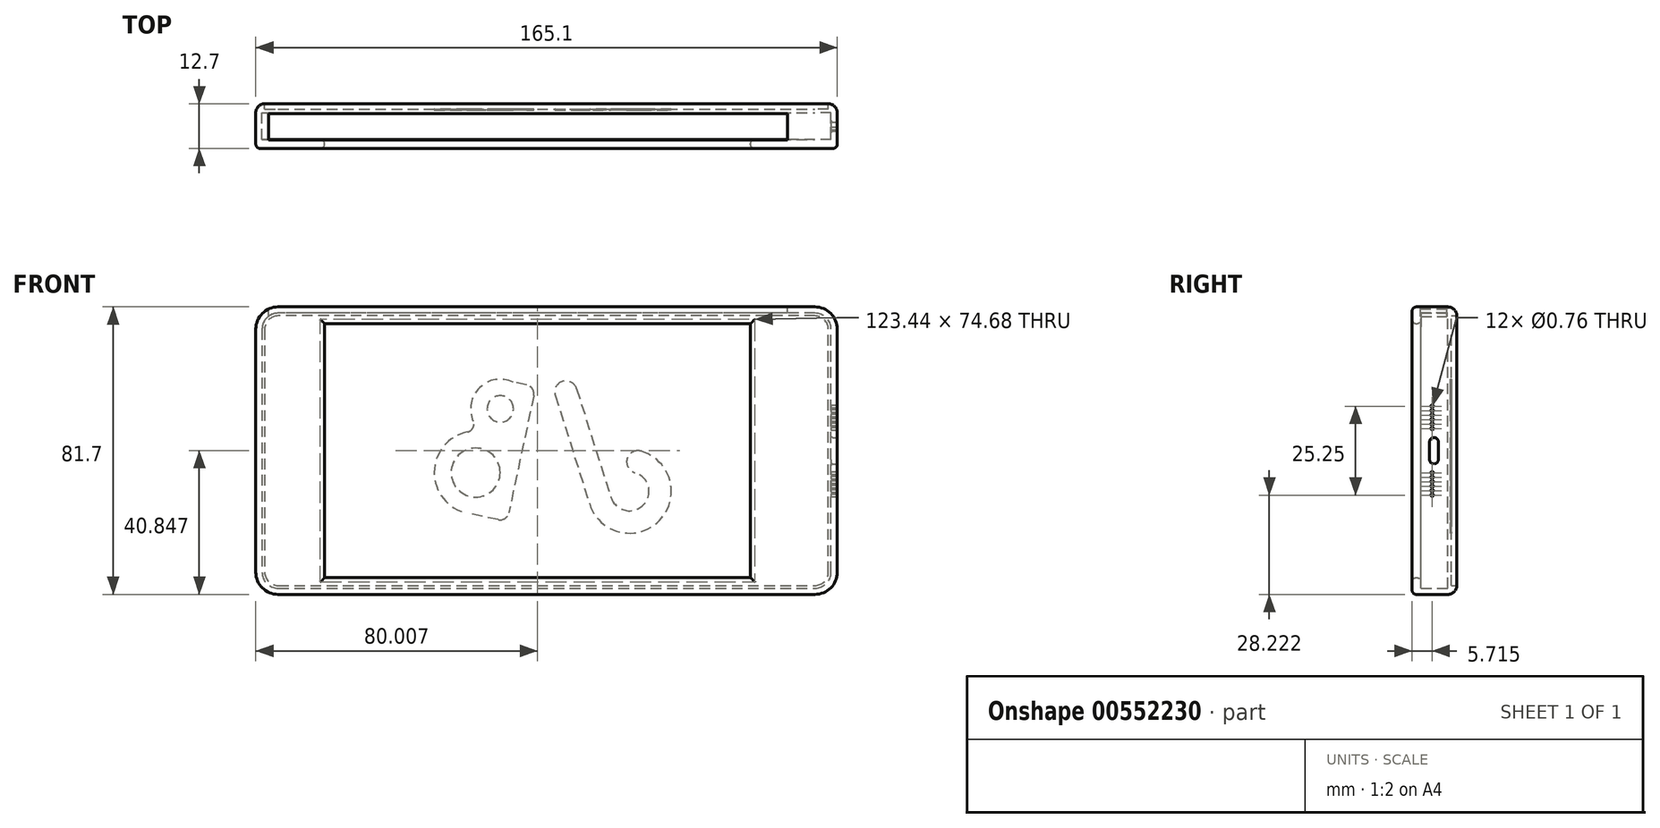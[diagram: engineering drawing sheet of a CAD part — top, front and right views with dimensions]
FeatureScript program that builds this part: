
annotation { "Feature Type Name" : "Feature", "Feature Type Description" : "" }
export const myFeature = defineFeature(function(context is Context, id is Id, definition is map)
    precondition{}
    {
        {
            var Q0;
            Q0=qCreatedBy(makeId("Front.planeOp"),FACE);
            var sketch = newSketch(context, id + "F0", { "sketchPlane" : qUnion([Q0])});
            skLineSegment(sketch, "E0", {"start": v(-49.18, 49.66) * mm, "end": v(-49.18, -19.34) * mm});
            skLineSegment(sketch, "E1", {"start": v(-42.83, -25.7) * mm, "end": v(109.57, -25.7) * mm});
            skLineSegment(sketch, "E2", {"start": v(115.92, -19.34) * mm, "end": v(115.92, 49.66) * mm});
            skLineSegment(sketch, "E3", {"start": v(109.57, 56) * mm, "end": v(-42.83, 56) * mm});
            skPoint(sketch, "E4.visualSharp", {"position": v(-49.18, 56) * mm});
            skArc(sketch, "E4.filletArc", {"start": v(-42.83, 56) * mm, "mid": v(-47.32, 54.15) * mm, "end": v(-49.18, 49.66) * mm});
            skPoint(sketch, "E5.visualSharp", {"position": v(-49.18, -25.7) * mm});
            skArc(sketch, "E5.filletArc", {"start": v(-49.18, -19.34) * mm, "mid": v(-47.32, -23.83) * mm, "end": v(-42.83, -25.7) * mm});
            skPoint(sketch, "E6.visualSharp", {"position": v(115.92, -25.7) * mm});
            skArc(sketch, "E6.filletArc", {"start": v(109.57, -25.7) * mm, "mid": v(114.06, -23.83) * mm, "end": v(115.92, -19.34) * mm});
            skPoint(sketch, "E7.visualSharp", {"position": v(115.92, 56) * mm});
            skArc(sketch, "E7.filletArc", {"start": v(115.92, 49.66) * mm, "mid": v(114.06, 54.15) * mm, "end": v(109.57, 56) * mm});
            skArc(sketch, "E8.0", {"start": v(114.14, 49.66) * mm, "mid": v(112.8, 52.89) * mm, "end": v(109.57, 54.23) * mm});
            skLineSegment(sketch, "E8.1", {"start": v(114.14, -19.34) * mm, "end": v(114.14, 49.66) * mm});
            skLineSegment(sketch, "E8.2", {"start": v(109.57, 54.23) * mm, "end": v(-42.83, 54.23) * mm});
            skArc(sketch, "E8.3", {"start": v(109.57, -23.91) * mm, "mid": v(112.8, -22.58) * mm, "end": v(114.14, -19.34) * mm});
            skArc(sketch, "E8.4", {"start": v(-42.83, 54.23) * mm, "mid": v(-46.07, 52.89) * mm, "end": v(-47.4, 49.66) * mm});
            skLineSegment(sketch, "E8.5", {"start": v(-47.4, 49.66) * mm, "end": v(-47.4, -19.34) * mm});
            skArc(sketch, "E8.6", {"start": v(-47.4, -19.34) * mm, "mid": v(-46.07, -22.58) * mm, "end": v(-42.83, -23.91) * mm});
            skLineSegment(sketch, "E8.7", {"start": v(-42.83, -23.91) * mm, "end": v(109.57, -23.91) * mm});
            skSolve(sketch);
        }
        {
            var Q0;
            Q0=makeQuery(id+"F0.imprint","IMPRINT",FACE,{"disambiguationData":[TD([[makeQuery(id+"F0.imprint","IMPRINT",EDGE,{"derivedFrom":sQuery(id+"F0.wireOp",EDGE,"E0")}),1.0]])]});
            extrude(context, id + "F1", {"entities" : qUnion([Q0]), "depth" : 12.7 * mm, "offsetDistance" : 25.4 * mm});
        }
        {
            var Q0;
            Q0=makeQuery(id+"F0.imprint","IMPRINT",FACE,{"disambiguationData":[TD([[makeQuery(id+"F0.imprint","IMPRINT",EDGE,{"derivedFrom":sQuery(id+"F0.wireOp",EDGE,"E8.0")}),1.0]])]});
            var Q1;
            Q1=makeQuery(id+"F1.opExtrude","CAP_FACE",FACE,{"disambiguationData":[OSD([sQuery(id+"F0.wireOp",EDGE,"E0"),sQuery(id+"F0.wireOp",EDGE,"E1"),sQuery(id+"F0.wireOp",EDGE,"E2"),sQuery(id+"F0.wireOp",EDGE,"E3"),sQuery(id+"F0.wireOp",EDGE,"E4.filletArc"),sQuery(id+"F0.wireOp",EDGE,"E5.filletArc"),sQuery(id+"F0.wireOp",EDGE,"E6.filletArc"),sQuery(id+"F0.wireOp",EDGE,"E7.filletArc"),sQuery(id+"F0.wireOp",EDGE,"E8.0"),sQuery(id+"F0.wireOp",EDGE,"E8.1"),sQuery(id+"F0.wireOp",EDGE,"E8.2"),sQuery(id+"F0.wireOp",EDGE,"E8.3"),sQuery(id+"F0.wireOp",EDGE,"E8.4"),sQuery(id+"F0.wireOp",EDGE,"E8.5"),sQuery(id+"F0.wireOp",EDGE,"E8.6"),sQuery(id+"F0.wireOp",EDGE,"E8.7")])],"isStart":false});
            extrude(context, id + "F2", {"entities" : qUnion([Q0]), "operationType" : NewBodyOperationType.ADD, "depth" : 2.54 * mm, "endBoundEntityFace" : qUnion([Q1]), "offsetDistance" : 25.4 * mm});
        }
        {
            var Q0;
            Q0=makeQuery(id+"F1.opExtrude","SWEPT_FACE",FACE,{"disambiguationData":[OSD([sQuery(id+"F0.wireOp",EDGE,"E3")])]});
            var sketch = newSketch(context, id + "F3", { "sketchPlane" : qUnion([Q0])});
            skLineSegment(sketch, "E9", {"start": v(-45.57, -2.8) * mm, "end": v(-45.57, -10.34) * mm});
            skLineSegment(sketch, "E10", {"start": v(-45.57, -10.34) * mm, "end": v(101.81, -10.34) * mm});
            skLineSegment(sketch, "E11", {"start": v(-45.57, -2.8) * mm, "end": v(101.81, -2.8) * mm});
            skLineSegment(sketch, "E12", {"start": v(101.81, -10.34) * mm, "end": v(101.81, -2.8) * mm});
            skSolve(sketch);
        }
        {
            var Q0;
            Q0 = qSketchRegion(id + "F3", true);
            extrude(context, id + "F4", {"entities" : qUnion([Q0]), "operationType" : NewBodyOperationType.REMOVE, "oppositeDirection" : true, "depth" : 25.4 * mm, "offsetDistance" : 25.4 * mm});
        }
        {
            var Q0;
            Q0=makeQuery(id+"F1.opExtrude","CAP_EDGE",EDGE,{"disambiguationData":[OSD([sQuery(id+"F0.wireOp",EDGE,"E7.filletArc")])],"isStart":true});
            fillet(context, id + "F5", {"entities" : qUnion([Q0]), "radius" : 2.54 * mm, "tangentPropagation" : true, "allowEdgeOverflow" : false});
        }
        {
            var Q0;
            Q0=makeQuery(id+"F1.opExtrude","CAP_EDGE",EDGE,{"disambiguationData":[OSD([sQuery(id+"F0.wireOp",EDGE,"E3")])],"isStart":false});
            var Q1;
            Q1=makeQuery(id+"F1.opExtrude","CAP_EDGE",EDGE,{"disambiguationData":[OSD([sQuery(id+"F0.wireOp",EDGE,"E1")])],"isStart":false});
            var Q2;
            Q2=makeQuery(id+"F1.opExtrude","CAP_EDGE",EDGE,{"disambiguationData":[OSD([sQuery(id+"F0.wireOp",EDGE,"E6.filletArc")])],"isStart":false});
            var Q3;
            Q3=makeQuery(id+"F1.opExtrude","CAP_EDGE",EDGE,{"disambiguationData":[OSD([sQuery(id+"F0.wireOp",EDGE,"E2")])],"isStart":false});
            var Q4;
            Q4=makeQuery(id+"F1.opExtrude","CAP_EDGE",EDGE,{"disambiguationData":[OSD([sQuery(id+"F0.wireOp",EDGE,"E7.filletArc")])],"isStart":false});
            var Q5;
            Q5=makeQuery(id+"F1.opExtrude","CAP_EDGE",EDGE,{"disambiguationData":[OSD([sQuery(id+"F0.wireOp",EDGE,"E4.filletArc")])],"isStart":false});
            var Q6;
            Q6=makeQuery(id+"F1.opExtrude","CAP_EDGE",EDGE,{"disambiguationData":[OSD([sQuery(id+"F0.wireOp",EDGE,"E5.filletArc")])],"isStart":false});
            fillet(context, id + "F6", {"entities" : qUnion([Q0, Q1, Q2, Q3, Q4, Q5, Q6]), "radius" : 1.27 * mm, "tangentPropagation" : true, "allowEdgeOverflow" : false});
        }
        {
            var Q0;
            {var subQ0=sQuery(id+"F0.wireOp",EDGE,"E8.7");var subQ1=sQuery(id+"F0.wireOp",EDGE,"E8.6");var subQ2=sQuery(id+"F0.wireOp",EDGE,"E8.5");var subQ3=sQuery(id+"F0.wireOp",EDGE,"E8.4");var subQ4=sQuery(id+"F0.wireOp",EDGE,"E8.3");var subQ5=sQuery(id+"F0.wireOp",EDGE,"E8.2");var subQ6=sQuery(id+"F0.wireOp",EDGE,"E8.1");var subQ7=sQuery(id+"F0.wireOp",EDGE,"E8.0");Q0=makeQuery(id+"F0kAOvEdBQfibV5_1.boolean.opBoolean","SPLIT",FACE,{"disambiguationData":[TD([makeQuery(id+"F0kAOvEdBQfibV5_1.opExtrude","SWEPT_FACE",FACE,{"disambiguationData":[OSD([sQuery(id+"FPcOAyLTUBux8Tv_1.wireOp",EDGE,"WfBB6rMJ-tLWI-lUQl-mpCu-Aw20YHy0fEWz")])]})])],"derivedFrom":makeQuery(id+"F2.boolean.opBoolean","MERGE",FACE,{"derivedFrom":[makeQuery(id+"F1.opExtrude","CAP_FACE",FACE,{"disambiguationData":[OSD([sQuery(id+"F0.wireOp",EDGE,"E0"),sQuery(id+"F0.wireOp",EDGE,"E1"),sQuery(id+"F0.wireOp",EDGE,"E2"),sQuery(id+"F0.wireOp",EDGE,"E3"),sQuery(id+"F0.wireOp",EDGE,"E4.filletArc"),sQuery(id+"F0.wireOp",EDGE,"E5.filletArc"),sQuery(id+"F0.wireOp",EDGE,"E6.filletArc"),sQuery(id+"F0.wireOp",EDGE,"E7.filletArc"),subQ7,subQ6,subQ5,subQ4,subQ3,subQ2,subQ1,subQ0])],"isStart":true}),makeQuery(id+"F2.opExtrude","CAP_FACE",FACE,{"disambiguationData":[OSD([subQ7,subQ6,subQ5,subQ4,subQ3,subQ2,subQ1,subQ0])],"isStart":true})]})});}
            var Q1;
            {var subQ0=sQuery(id+"F0.wireOp",EDGE,"E8.7");var subQ1=sQuery(id+"F0.wireOp",EDGE,"E8.6");var subQ2=sQuery(id+"F0.wireOp",EDGE,"E8.5");var subQ3=sQuery(id+"F0.wireOp",EDGE,"E8.4");var subQ4=sQuery(id+"F0.wireOp",EDGE,"E8.3");var subQ5=sQuery(id+"F0.wireOp",EDGE,"E8.2");var subQ6=sQuery(id+"F0.wireOp",EDGE,"E8.1");var subQ7=sQuery(id+"F0.wireOp",EDGE,"E8.0");Q1=makeQuery(id+"F0kAOvEdBQfibV5_1.boolean.opBoolean","SPLIT",FACE,{"disambiguationData":[TD([makeQuery(id+"F0kAOvEdBQfibV5_1.opExtrude","SWEPT_FACE",FACE,{"disambiguationData":[OSD([sQuery(id+"FPcOAyLTUBux8Tv_1.wireOp",EDGE,"bPc5HWd9-vX2H-GCn0-Inl4-AklKT95ZlBm9")])]})])],"derivedFrom":makeQuery(id+"F2.boolean.opBoolean","MERGE",FACE,{"derivedFrom":[makeQuery(id+"F1.opExtrude","CAP_FACE",FACE,{"disambiguationData":[OSD([sQuery(id+"F0.wireOp",EDGE,"E0"),sQuery(id+"F0.wireOp",EDGE,"E1"),sQuery(id+"F0.wireOp",EDGE,"E2"),sQuery(id+"F0.wireOp",EDGE,"E3"),sQuery(id+"F0.wireOp",EDGE,"E4.filletArc"),sQuery(id+"F0.wireOp",EDGE,"E5.filletArc"),sQuery(id+"F0.wireOp",EDGE,"E6.filletArc"),sQuery(id+"F0.wireOp",EDGE,"E7.filletArc"),subQ7,subQ6,subQ5,subQ4,subQ3,subQ2,subQ1,subQ0])],"isStart":true}),makeQuery(id+"F2.opExtrude","CAP_FACE",FACE,{"disambiguationData":[OSD([subQ7,subQ6,subQ5,subQ4,subQ3,subQ2,subQ1,subQ0])],"isStart":true})]})});}
            extrude(context, id + "F7", {"entities" : qUnion([Q0, Q1]), "operationType" : NewBodyOperationType.REMOVE, "oppositeDirection" : true, "depth" : 1.52 * mm, "offsetDistance" : 25.4 * mm});
        }
        {
            var Q0;
            Q0=makeQuery(id+"F1.opExtrude","CAP_EDGE",EDGE,{"disambiguationData":[OSD([sQuery(id+"F0.wireOp",EDGE,"E8.2")])],"isStart":false});
            cPlane(context, id + "F8", {"entities" : qUnion([Q0]), "cplaneType" : CPlaneType.LINE_ANGLE, "offset" : 25.4 * mm, "angle" : 0 * degree, "width" : 152.4 * mm, "height" : 152.4 * mm});
        }
        {
            var Q0;
            Q0=qCreatedBy(id+"F8.planeOp",FACE);
            var sketch = newSketch(context, id + "F9", { "sketchPlane" : qUnion([Q0])});
            skLineSegment(sketch, "E13.0", {"start": v(-47.4, 49.66) * mm, "end": v(-47.4, -19.34) * mm});
            skArc(sketch, "E14.0", {"start": v(-42.83, 54.23) * mm, "mid": v(-46.07, 52.89) * mm, "end": v(-47.4, 49.66) * mm});
            skLineSegment(sketch, "E15.0", {"start": v(109.57, 54.23) * mm, "end": v(-42.83, 54.23) * mm});
            skArc(sketch, "E16.0", {"start": v(114.14, 49.66) * mm, "mid": v(112.8, 52.89) * mm, "end": v(109.57, 54.23) * mm});
            skLineSegment(sketch, "E17.0", {"start": v(114.14, -19.34) * mm, "end": v(114.14, 49.66) * mm});
            skArc(sketch, "E18.0", {"start": v(109.57, -23.91) * mm, "mid": v(112.8, -22.58) * mm, "end": v(114.14, -19.34) * mm});
            skLineSegment(sketch, "E19.0", {"start": v(-42.83, -23.91) * mm, "end": v(109.57, -23.91) * mm});
            skArc(sketch, "E20.0", {"start": v(-47.4, -19.34) * mm, "mid": v(-46.07, -22.58) * mm, "end": v(-42.83, -23.91) * mm});
            skLineSegment(sketch, "E21.0", {"start": v(91.28, 51.23) * mm, "end": v(-29.62, 51.23) * mm});
            skLineSegment(sketch, "E22.0", {"start": v(-29.62, -20.91) * mm, "end": v(91.28, -20.91) * mm});
            skLineSegment(sketch, "E23", {"start": v(-29.62, -20.91) * mm, "end": v(-29.62, 51.23) * mm});
            skLineSegment(sketch, "E24", {"start": v(91.28, 51.23) * mm, "end": v(91.28, -20.91) * mm});
            skPoint(sketch, "E24.endSnap0", {"position": v(-46.07, -22.58) * mm});
            skSolve(sketch);
        }
        {
            var Q0;
            Q0 = qSketchRegion(id + "F9", true);
            extrude(context, id + "F10", {"entities" : qUnion([Q0]), "operationType" : NewBodyOperationType.ADD, "oppositeDirection" : true, "depth" : 2.54 * mm, "offsetDistance" : 25.4 * mm});
        }
        {
            var Q0;
            Q0=makeQuery(id+"F1.opExtrude","SWEPT_FACE",FACE,{"disambiguationData":[OSD([sQuery(id+"F0.wireOp",EDGE,"E2")])]});
            var sketch = newSketch(context, id + "F11", { "sketchPlane" : qUnion([Q0])});
            skLineSegment(sketch, "E25", {"start": v(-6.48, 18.9) * mm, "end": v(-6.48, 18.9) * mm});
            skLineSegment(sketch, "E26", {"start": v(-5.2, 17.62) * mm, "end": v(-5.2, 12.7) * mm});
            skLineSegment(sketch, "E27", {"start": v(-7.75, 17.62) * mm, "end": v(-7.75, 12.7) * mm});
            skLineSegment(sketch, "E28", {"start": v(-6.48, 11.42) * mm, "end": v(-6.48, 11.42) * mm});
            skCircle(sketch, "E29", {"center": v(-6.99, 21.43) * mm, "radius": 0.38 * mm});
            skCircle(sketch, "E30", {"center": v(-6.99, 22.7) * mm, "radius": 0.38 * mm});
            skCircle(sketch, "E31", {"center": v(-6.99, 23.97) * mm, "radius": 0.38 * mm});
            skCircle(sketch, "E32", {"center": v(-6.99, 25.24) * mm, "radius": 0.38 * mm});
            skCircle(sketch, "E33", {"center": v(-6.99, 26.51) * mm, "radius": 0.38 * mm});
            skCircle(sketch, "E34", {"center": v(-6.99, 27.78) * mm, "radius": 0.38 * mm});
            skCircle(sketch, "E35", {"center": v(-6.99, 8.88) * mm, "radius": 0.38 * mm});
            skCircle(sketch, "E36", {"center": v(-6.99, 7.61) * mm, "radius": 0.38 * mm});
            skCircle(sketch, "E37", {"center": v(-6.99, 6.34) * mm, "radius": 0.38 * mm});
            skCircle(sketch, "E38", {"center": v(-6.98, 5.07) * mm, "radius": 0.38 * mm});
            skCircle(sketch, "E39", {"center": v(-6.99, 3.8) * mm, "radius": 0.38 * mm});
            skLineSegment(sketch, "E40", {"start": v(-7.75, 15.16) * mm, "end": v(-5.2, 15.16) * mm});
            skLineSegment(sketch, "E41", {"start": v(-6.99, 49.66) * mm, "end": v(-6.98, -19.34) * mm});
            skLineSegment(sketch, "E42", {"start": v(-11.43, 15.16) * mm, "end": v(-1.52, 15.16) * mm});
            skLineSegment(sketch, "E43", {"start": v(-7.75, 17.62) * mm, "end": v(-7.75, 17.62) * mm});
            skLineSegment(sketch, "E44", {"start": v(-7.75, 12.7) * mm, "end": v(-7.75, 12.7) * mm});
            skLineSegment(sketch, "E45", {"start": v(-5.2, 17.62) * mm, "end": v(-5.2, 17.62) * mm});
            skLineSegment(sketch, "E46", {"start": v(-5.2, 12.7) * mm, "end": v(-5.2, 12.7) * mm});
            skPoint(sketch, "E47", {"position": v(-6.48, 11.42) * mm});
            skCircle(sketch, "E48", {"center": v(-6.99, 2.53) * mm, "radius": 0.38 * mm});
            skPoint(sketch, "E49.visualSharp", {"position": v(-7.75, 18.9) * mm});
            skArc(sketch, "E49.filletArc", {"start": v(-6.48, 18.9) * mm, "mid": v(-7.38, 18.52) * mm, "end": v(-7.75, 17.62) * mm});
            skPoint(sketch, "E50.visualSharp", {"position": v(-5.2, 18.9) * mm});
            skArc(sketch, "E50.filletArc", {"start": v(-5.2, 17.62) * mm, "mid": v(-5.58, 18.52) * mm, "end": v(-6.48, 18.9) * mm});
            skPoint(sketch, "E51.visualSharp", {"position": v(-5.2, 11.42) * mm});
            skArc(sketch, "E51.filletArc", {"start": v(-6.48, 11.42) * mm, "mid": v(-5.58, 11.8) * mm, "end": v(-5.2, 12.7) * mm});
            skPoint(sketch, "E52.visualSharp", {"position": v(-7.75, 11.42) * mm});
            skArc(sketch, "E52.filletArc", {"start": v(-7.75, 12.7) * mm, "mid": v(-7.38, 11.8) * mm, "end": v(-6.48, 11.42) * mm});
            skSolve(sketch);
        }
        {
            var Q0;
            Q0 = qSketchRegion(id + "F11", true);
            extrude(context, id + "F12", {"entities" : qUnion([Q0]), "operationType" : NewBodyOperationType.REMOVE, "oppositeDirection" : true, "depth" : 25.4 * mm, "offsetDistance" : 25.4 * mm});
        }
        {
            var Q0;
            Q0=makeQuery(id+"F12.boolean.opBoolean","COPY",EDGE,{"derivedFrom":makeQuery(id+"F12.opExtrude","CAP_EDGE",EDGE,{"disambiguationData":[OSD([sQuery(id+"F11.wireOp",EDGE,"E27")])],"isStart":true})});
            var Q1;
            Q1=makeQuery(id+"F12.boolean.opBoolean","INTERSECT",EDGE,{"derivedFrom":[makeQuery(id+"F1.opExtrude","SWEPT_FACE",FACE,{"disambiguationData":[OSD([sQuery(id+"F0.wireOp",EDGE,"E8.1")])]}),makeQuery(id+"F12.opExtrude","SWEPT_FACE",FACE,{"disambiguationData":[OSD([sQuery(id+"F11.wireOp",EDGE,"E26")])]})]});
            fillet(context, id + "F13", {"entities" : qUnion([Q0, Q1]), "radius" : 0.5 * mm, "tangentPropagation" : true, "allowEdgeOverflow" : false});
        }
        {
            var Q0;
            Q0=makeQuery(id+"F7.boolean.opBoolean","COPY",FACE,{"derivedFrom":makeQuery(id+"F7.opExtrude","CAP_FACE",FACE,{"disambiguationData":[OSD([sQuery(id+"F0.wireOp",EDGE,"E0"),sQuery(id+"F0.wireOp",EDGE,"E1"),sQuery(id+"F0.wireOp",EDGE,"E2"),sQuery(id+"F0.wireOp",EDGE,"E3"),sQuery(id+"F0.wireOp",EDGE,"E4.filletArc"),sQuery(id+"F0.wireOp",EDGE,"E5.filletArc"),sQuery(id+"F0.wireOp",EDGE,"E6.filletArc"),sQuery(id+"F0.wireOp",EDGE,"E7.filletArc"),sQuery(id+"F0.wireOp",EDGE,"E8.0"),sQuery(id+"F0.wireOp",EDGE,"E8.1"),sQuery(id+"F0.wireOp",EDGE,"E8.2"),sQuery(id+"F0.wireOp",EDGE,"E8.3"),sQuery(id+"F0.wireOp",EDGE,"E8.4"),sQuery(id+"F0.wireOp",EDGE,"E8.5"),sQuery(id+"F0.wireOp",EDGE,"E8.6"),sQuery(id+"F0.wireOp",EDGE,"E8.7")])],"isStart":false})});
            var sketch = newSketch(context, id + "F14", { "sketchPlane" : qUnion([Q0])});
            skLineSegment(sketch, "E53", {"start": v(-35.84, 30.85) * mm, "end": v(-45.59, 0.02) * mm});
            skArc(sketch, "E54", {"start": v(-45.59, 0.02) * mm, "mid": v(-65.45, -4.67) * mm, "end": v(-60.14, 15.03) * mm});
            skArc(sketch, "E55.0", {"start": v(-51.65, 1.93) * mm, "mid": v(-60.89, -0.25) * mm, "end": v(-58.42, 8.92) * mm});
            skLineSegment(sketch, "E55.1", {"start": v(-41.9, 32.77) * mm, "end": v(-51.65, 1.93) * mm});
            skArc(sketch, "E56", {"start": v(-58.42, 8.92) * mm, "mid": v(-56.22, 12.84) * mm, "end": v(-60.14, 15.03) * mm});
            skArc(sketch, "E57", {"start": v(-35.84, 30.85) * mm, "mid": v(-37.92, 34.84) * mm, "end": v(-41.9, 32.77) * mm});
            skLineSegment(sketch, "E58", {"start": v(-29.72, 30.8) * mm, "end": v(-22.65, -2.49) * mm});
            skLineSegment(sketch, "E59", {"start": v(-19.64, -4.45) * mm, "end": v(-10.8, -2.57) * mm});
            skLineSegment(sketch, "E60", {"start": v(-27.76, 33.82) * mm, "end": v(-23.88, 34.64) * mm});
            skArc(sketch, "E61", {"start": v(-10.8, -2.57) * mm, "mid": v(-1.48, 9) * mm, "end": v(-10.94, 20.48) * mm});
            skPoint(sketch, "E61.third.point", {"position": v(-24.98, 8.5) * mm});
            skArc(sketch, "E62", {"start": v(-12.55, 23.6) * mm, "mid": v(-14.36, 33.06) * mm, "end": v(-23.88, 34.64) * mm});
            skPoint(sketch, "E62.second.point", {"position": v(-11.87, 26.05) * mm});
            skPoint(sketch, "E62.third.point", {"position": v(-14.77, 20.61) * mm});
            skPoint(sketch, "E63.visualSharp", {"position": v(-30.24, 33.29) * mm});
            skArc(sketch, "E63.filletArc", {"start": v(-27.76, 33.82) * mm, "mid": v(-29.36, 32.72) * mm, "end": v(-29.72, 30.8) * mm});
            skPoint(sketch, "E64.visualSharp", {"position": v(-19.98, 18.6) * mm});
            skArc(sketch, "E64.filletArc", {"start": v(-12.55, 23.6) * mm, "mid": v(-12.49, 21.65) * mm, "end": v(-10.94, 20.48) * mm});
            skCircle(sketch, "E65", {"center": v(-20.25, 27.02) * mm, "radius": 3.76 * mm});
            skCircle(sketch, "E66", {"center": v(-13.25, 8.94) * mm, "radius": 6.96 * mm});
            skPoint(sketch, "E67.visualSharp", {"position": v(-22.13, -4.97) * mm});
            skArc(sketch, "E67.filletArc", {"start": v(-22.65, -2.49) * mm, "mid": v(-21.55, -4.1) * mm, "end": v(-19.64, -4.45) * mm});
            skSolve(sketch);
        }
        {
            var Q0;
            Q0=makeQuery(id+"F14.imprint","IMPRINT",FACE,{"disambiguationData":[TD([[makeQuery(id+"F14.imprint","IMPRINT",EDGE,{"derivedFrom":sQuery(id+"F14.wireOp",EDGE,"E53")}),-1.0]])]});
            var Q1;
            Q1=makeQuery(id+"F14.imprint","IMPRINT",FACE,{"disambiguationData":[TD([[makeQuery(id+"F14.imprint","IMPRINT",EDGE,{"derivedFrom":sQuery(id+"F14.wireOp",EDGE,"E58")}),1.0]])]});
            extrude(context, id + "F15", {"entities" : qUnion([Q0, Q1]), "operationType" : NewBodyOperationType.REMOVE, "oppositeDirection" : true, "depth" : 0.25 * mm, "offsetDistance" : 25.4 * mm});
        }
        {
            var Q0;
            Q0=makeQuery(id+"F15.boolean.opBoolean","SPLIT",FACE,{"disambiguationData":[TD([makeQuery(id+"F15.opExtrude","SWEPT_FACE",FACE,{"disambiguationData":[OSD([sQuery(id+"F14.wireOp",EDGE,"E65")])]})])],"derivedFrom":makeQuery(id+"F7.boolean.opBoolean","COPY",FACE,{"derivedFrom":makeQuery(id+"F7.opExtrude","CAP_FACE",FACE,{"disambiguationData":[OSD([sQuery(id+"F0.wireOp",EDGE,"E0"),sQuery(id+"F0.wireOp",EDGE,"E1"),sQuery(id+"F0.wireOp",EDGE,"E2"),sQuery(id+"F0.wireOp",EDGE,"E3"),sQuery(id+"F0.wireOp",EDGE,"E4.filletArc"),sQuery(id+"F0.wireOp",EDGE,"E5.filletArc"),sQuery(id+"F0.wireOp",EDGE,"E6.filletArc"),sQuery(id+"F0.wireOp",EDGE,"E7.filletArc"),sQuery(id+"F0.wireOp",EDGE,"E8.0"),sQuery(id+"F0.wireOp",EDGE,"E8.1"),sQuery(id+"F0.wireOp",EDGE,"E8.2"),sQuery(id+"F0.wireOp",EDGE,"E8.3"),sQuery(id+"F0.wireOp",EDGE,"E8.4"),sQuery(id+"F0.wireOp",EDGE,"E8.5"),sQuery(id+"F0.wireOp",EDGE,"E8.6"),sQuery(id+"F0.wireOp",EDGE,"E8.7")])],"isStart":false})})});
            var Q1;
            Q1=makeQuery(id+"F15.boolean.opBoolean","SPLIT",FACE,{"disambiguationData":[TD([makeQuery(id+"F15.opExtrude","SWEPT_FACE",FACE,{"disambiguationData":[OSD([sQuery(id+"F14.wireOp",EDGE,"E66")])]})])],"derivedFrom":makeQuery(id+"F7.boolean.opBoolean","COPY",FACE,{"derivedFrom":makeQuery(id+"F7.opExtrude","CAP_FACE",FACE,{"disambiguationData":[OSD([sQuery(id+"F0.wireOp",EDGE,"E0"),sQuery(id+"F0.wireOp",EDGE,"E1"),sQuery(id+"F0.wireOp",EDGE,"E2"),sQuery(id+"F0.wireOp",EDGE,"E3"),sQuery(id+"F0.wireOp",EDGE,"E4.filletArc"),sQuery(id+"F0.wireOp",EDGE,"E5.filletArc"),sQuery(id+"F0.wireOp",EDGE,"E6.filletArc"),sQuery(id+"F0.wireOp",EDGE,"E7.filletArc"),sQuery(id+"F0.wireOp",EDGE,"E8.0"),sQuery(id+"F0.wireOp",EDGE,"E8.1"),sQuery(id+"F0.wireOp",EDGE,"E8.2"),sQuery(id+"F0.wireOp",EDGE,"E8.3"),sQuery(id+"F0.wireOp",EDGE,"E8.4"),sQuery(id+"F0.wireOp",EDGE,"E8.5"),sQuery(id+"F0.wireOp",EDGE,"E8.6"),sQuery(id+"F0.wireOp",EDGE,"E8.7")])],"isStart":false})})});
            extrude(context, id + "F16", {"entities" : qUnion([Q0, Q1]), "operationType" : NewBodyOperationType.REMOVE, "oppositeDirection" : true, "depth" : 0.13 * mm, "offsetDistance" : 25.4 * mm});
        }
        {
            var Q0;
            Q0=makeQuery(id+"F10.opExtrude","CAP_EDGE",EDGE,{"disambiguationData":[OSD([sQuery(id+"F9.wireOp",EDGE,"E23")])],"isStart":true});
            var Q1;
            Q1=makeQuery(id+"F10.opExtrude","CAP_EDGE",EDGE,{"disambiguationData":[OSD([sQuery(id+"F9.wireOp",EDGE,"E21.0")])],"isStart":true});
            var Q2;
            Q2=makeQuery(id+"F10.opExtrude","CAP_EDGE",EDGE,{"disambiguationData":[OSD([sQuery(id+"F9.wireOp",EDGE,"E24")])],"isStart":true});
            var Q3;
            Q3=makeQuery(id+"F10.opExtrude","CAP_EDGE",EDGE,{"disambiguationData":[OSD([sQuery(id+"F9.wireOp",EDGE,"E22.0")])],"isStart":true});
            var Q4;
            Q4=makeQuery(id+"F10.opExtrude","CAP_EDGE",EDGE,{"disambiguationData":[OSD([sQuery(id+"F9.wireOp",EDGE,"E23")])],"isStart":false});
            var Q5;
            Q5=makeQuery(id+"F10.opExtrude","CAP_EDGE",EDGE,{"disambiguationData":[OSD([sQuery(id+"F9.wireOp",EDGE,"E21.0")])],"isStart":false});
            var Q6;
            Q6=makeQuery(id+"F10.opExtrude","CAP_EDGE",EDGE,{"disambiguationData":[OSD([sQuery(id+"F9.wireOp",EDGE,"E24")])],"isStart":false});
            var Q7;
            Q7=makeQuery(id+"F10.opExtrude","CAP_EDGE",EDGE,{"disambiguationData":[OSD([sQuery(id+"F9.wireOp",EDGE,"E22.0")])],"isStart":false});
            fillet(context, id + "F17", {"entities" : qUnion([Q0, Q1, Q2, Q3, Q4, Q5, Q6, Q7]), "radius" : 1.27 * mm, "tangentPropagation" : true, "allowEdgeOverflow" : false});
        }
    });
